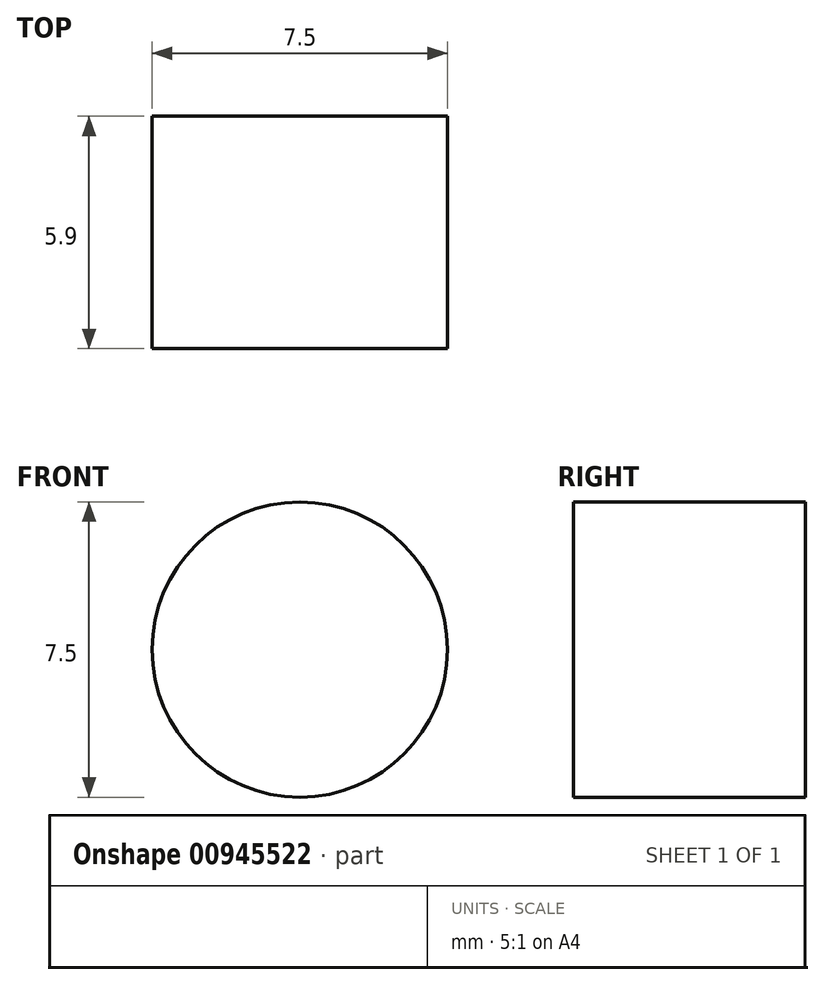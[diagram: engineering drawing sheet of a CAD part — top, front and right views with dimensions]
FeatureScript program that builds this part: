
annotation { "Feature Type Name" : "Feature", "Feature Type Description" : "" }
export const myFeature = defineFeature(function(context is Context, id is Id, definition is map)
    precondition{}
    {
        {
            var Q0;
            Q0=qCreatedBy(makeId("Front.planeOp"),FACE);
            var sketch = newSketch(context, id + "F0", { "sketchPlane" : qUnion([Q0])});
            skCircle(sketch, "E0", {"center": v(0, 0) * mm, "radius": 3.75 * mm});
            skSolve(sketch);
        }
        {
            var Q0;
            Q0 = qSketchRegion(id + "F0", true);
            extrude(context, id + "F1", {"entities" : qUnion([Q0]), "endBound" : BoundingType.SYMMETRIC, "depth" : 5.9 * mm, "offsetDistance" : 25.4 * mm});
        }
    });
